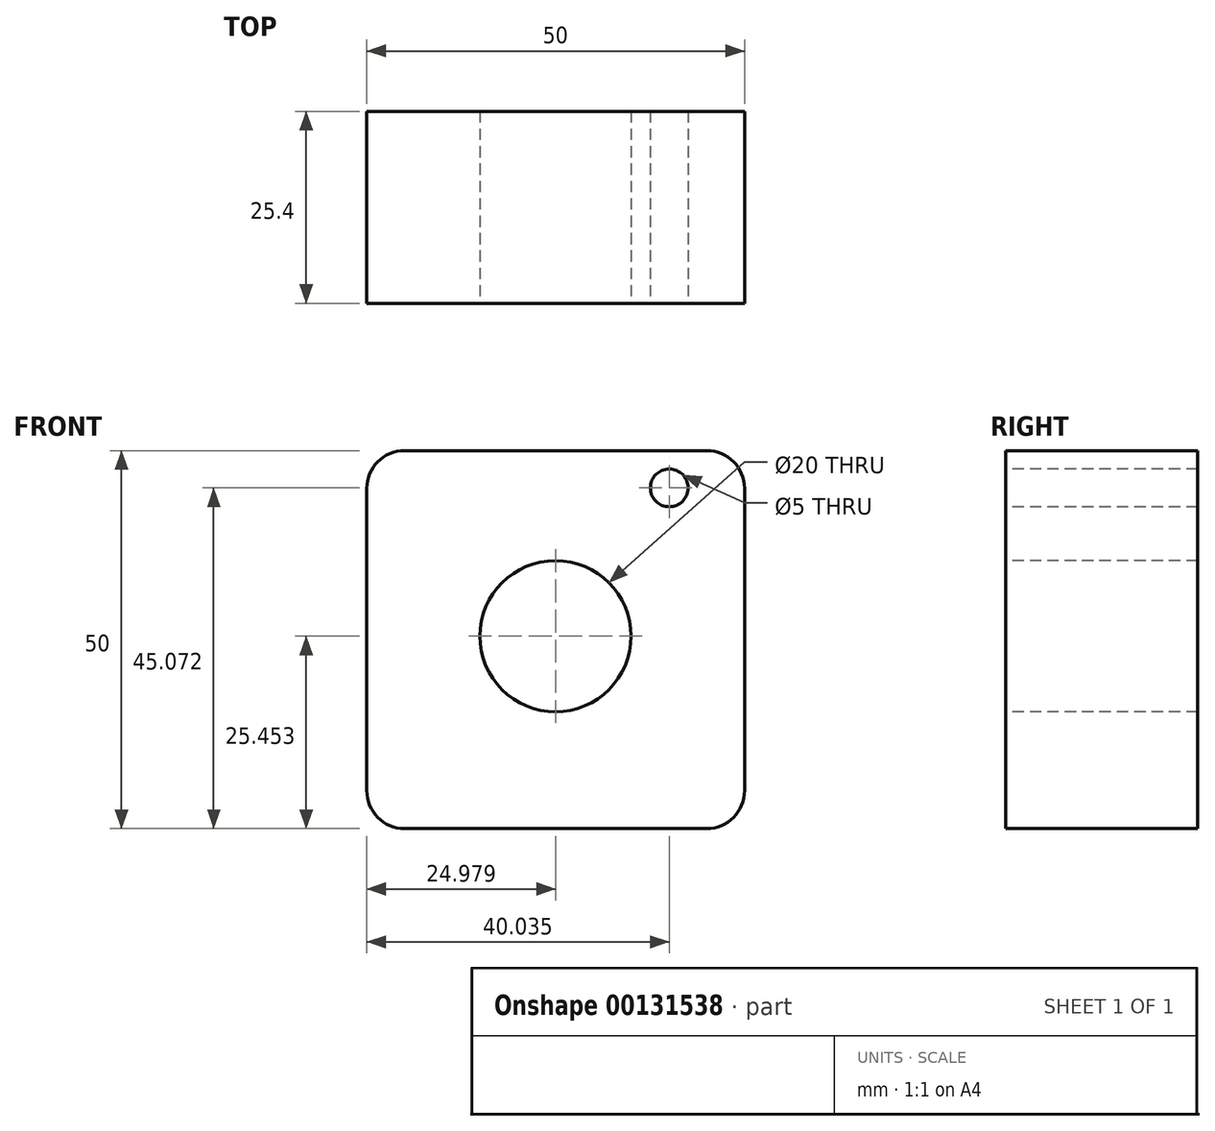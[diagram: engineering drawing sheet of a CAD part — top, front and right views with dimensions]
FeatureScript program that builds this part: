
annotation { "Feature Type Name" : "Feature", "Feature Type Description" : "" }
export const myFeature = defineFeature(function(context is Context, id is Id, definition is map)
    precondition{}
    {
        {
            var Q0;
            Q0=qCreatedBy(makeId("Front.planeOp"),FACE);
            var sketch = newSketch(context, id + "F0", { "sketchPlane" : qUnion([Q0])});
            skLineSegment(sketch, "E0.bottom", {"start": v(0, 50) * mm, "end": v(50, 50) * mm});
            skLineSegment(sketch, "E0.top", {"start": v(0, 0) * mm, "end": v(50, 0) * mm});
            skLineSegment(sketch, "E0.left", {"start": v(0, 50) * mm, "end": v(0, 0) * mm});
            skLineSegment(sketch, "E0.right", {"start": v(50, 50) * mm, "end": v(50, 0) * mm});
            skSolve(sketch);
        }
        {
            var Q0;
            Q0=makeQuery(id+"F0.imprint","IMPRINT",FACE,{"disambiguationData":[TD([[makeQuery(id+"F0.imprint","IMPRINT",EDGE,{"derivedFrom":sQuery(id+"F0.wireOp",EDGE,"E0.bottom")}),-1.0]])]});
            extrude(context, id + "F1", {"entities" : qUnion([Q0]), "depth" : 25.4 * mm});
        }
        {
            var Q0;
            Q0=makeQuery(id+"F1.opExtrude","CAP_FACE",FACE,{"disambiguationData":[OSD([sQuery(id+"F0.wireOp",EDGE,"E0.bottom"),sQuery(id+"F0.wireOp",EDGE,"E0.top"),sQuery(id+"F0.wireOp",EDGE,"E0.left"),sQuery(id+"F0.wireOp",EDGE,"E0.right")])],"isStart":false});
            var sketch = newSketch(context, id + "F2", { "sketchPlane" : qUnion([Q0])});
            skPoint(sketch, "E1", {"position": v(24.98, 25.45) * mm});
            skSolve(sketch);
        }
        {
            var Q0;
            Q0=sQuery(id+"F2.wireOp",VERTEX,"E1");
            var Q1;
            Q1=makeQuery(id+"F1.opExtrude","SWEPT_BODY",BODY,{"disambiguationData":[OSD([sQuery(id+"F0.wireOp",EDGE,"E0.bottom"),sQuery(id+"F0.wireOp",EDGE,"E0.top"),sQuery(id+"F0.wireOp",EDGE,"E0.left"),sQuery(id+"F0.wireOp",EDGE,"E0.right")])]});
            hole(context, id + "F3", {"style" : HoleStyle.SIMPLE, "endStyle" : HoleEndStyle.THROUGH, "holeDiameter" : 20 * mm, "locations" : qUnion([Q0]), "scope" : qUnion([Q1]), "isTappedThrough" : true});
        }
        {
            var Q0;
            Q0=makeQuery(id+"F1.opExtrude","SWEPT_EDGE",EDGE,{"disambiguationData":[OSD([sQuery(id+"F0.wireOp",EDGE,"E0.bottom"),sQuery(id+"F0.wireOp",EDGE,"E0.right")])]});
            var Q1;
            Q1=makeQuery(id+"F1.opExtrude","SWEPT_EDGE",EDGE,{"disambiguationData":[OSD([sQuery(id+"F0.wireOp",EDGE,"E0.top"),sQuery(id+"F0.wireOp",EDGE,"E0.right")])]});
            var Q2;
            Q2=makeQuery(id+"F3.hole-0.boolean.opBoolean","COPY",EDGE,{"derivedFrom":makeQuery(id+"F3.hole-0.opRevolve","SWEPT_EDGE",EDGE,{"disambiguationData":[OSD([sQuery(id+"F3.hole-0.sketch.wireOp",EDGE,"core_line_2"),sQuery(id+"F3.hole-0.sketch.wireOp",EDGE,"core_line_3")])]})});
            var Q3;
            Q3=makeQuery(id+"F3.hole-0.boolean.opBoolean","INTERSECT",EDGE,{"derivedFrom":[makeQuery(id+"F1.opExtrude","CAP_FACE",FACE,{"disambiguationData":[OSD([sQuery(id+"F0.wireOp",EDGE,"E0.bottom"),sQuery(id+"F0.wireOp",EDGE,"E0.top"),sQuery(id+"F0.wireOp",EDGE,"E0.left"),sQuery(id+"F0.wireOp",EDGE,"E0.right")])],"isStart":true}),makeQuery(id+"F3.hole-0.opRevolve","SWEPT_FACE",FACE,{"disambiguationData":[OSD([sQuery(id+"F3.hole-0.sketch.wireOp",EDGE,"core_line_2")])]})]});
            var Q4;
            Q4=makeQuery(id+"F1.opExtrude","SWEPT_EDGE",EDGE,{"disambiguationData":[OSD([sQuery(id+"F0.wireOp",EDGE,"E0.bottom"),sQuery(id+"F0.wireOp",EDGE,"E0.left")])]});
            var Q5;
            Q5=makeQuery(id+"F1.opExtrude","SWEPT_EDGE",EDGE,{"disambiguationData":[OSD([sQuery(id+"F0.wireOp",EDGE,"E0.top"),sQuery(id+"F0.wireOp",EDGE,"E0.left")])]});
            fillet(context, id + "F4", {"entities" : qUnion([Q0, Q1, Q2, Q3, Q4, Q5]), "radius" : 5 * mm, "tangentPropagation" : true, "allowEdgeOverflow" : false});
        }
        {
            var Q0;
            Q0=makeQuery(id+"F1.opExtrude","CAP_FACE",FACE,{"disambiguationData":[OSD([sQuery(id+"F0.wireOp",EDGE,"E0.bottom"),sQuery(id+"F0.wireOp",EDGE,"E0.top"),sQuery(id+"F0.wireOp",EDGE,"E0.left"),sQuery(id+"F0.wireOp",EDGE,"E0.right")])],"isStart":false});
            var sketch = newSketch(context, id + "F5", { "sketchPlane" : qUnion([Q0])});
            skPoint(sketch, "E2", {"position": v(40, 40) * mm});
            skPoint(sketch, "E3", {"position": v(50, 37.7) * mm});
            skPoint(sketch, "E4", {"position": v(40.04, 45.07) * mm});
            skSolve(sketch);
        }
        {
            var Q0;
            Q0=sQuery(id+"F5.wireOp",VERTEX,"E4");
            var Q1;
            Q1=makeQuery(id+"F1.opExtrude","SWEPT_BODY",BODY,{"disambiguationData":[OSD([sQuery(id+"F0.wireOp",EDGE,"E0.bottom"),sQuery(id+"F0.wireOp",EDGE,"E0.top"),sQuery(id+"F0.wireOp",EDGE,"E0.left"),sQuery(id+"F0.wireOp",EDGE,"E0.right")])]});
            hole(context, id + "F6", {"style" : HoleStyle.SIMPLE, "endStyle" : HoleEndStyle.THROUGH, "holeDiameter" : 5 * mm, "locations" : qUnion([Q0]), "scope" : qUnion([Q1]), "isTappedThrough" : true});
        }
    });
